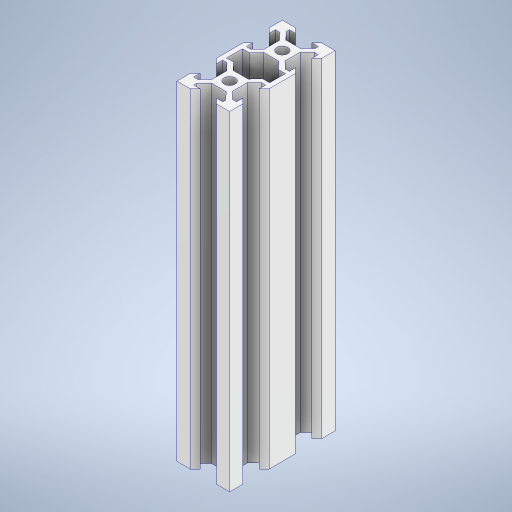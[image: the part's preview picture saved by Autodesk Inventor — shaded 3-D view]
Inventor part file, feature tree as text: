
AUTODESK INVENTOR PART (.ipt)
format: ipt  version: 2023 (Build 270158000, 158)  size: 326,144 bytes
history: native  units: mm
features: extrude x1, sketch x1
ambient origin geometry x8: Origin, YZ Plane, XZ Plane, XY Plane, X Axis, Y Axis, Z Axis, Center Point
bodies: Solid2 (feature_tree), Solid1 (feature_tree)
feature tree (2):
  extrude  "Extrusion1"  [1 undecoded]
  sketch  "Sketch1"  dims[d0=150.0mm d1=0.0mm]
note: 1 required parameter value undecoded (feature->parameter linkage not recoverable at this tier; creation-order binding heuristic only, values carry confidence <= 0.55)
